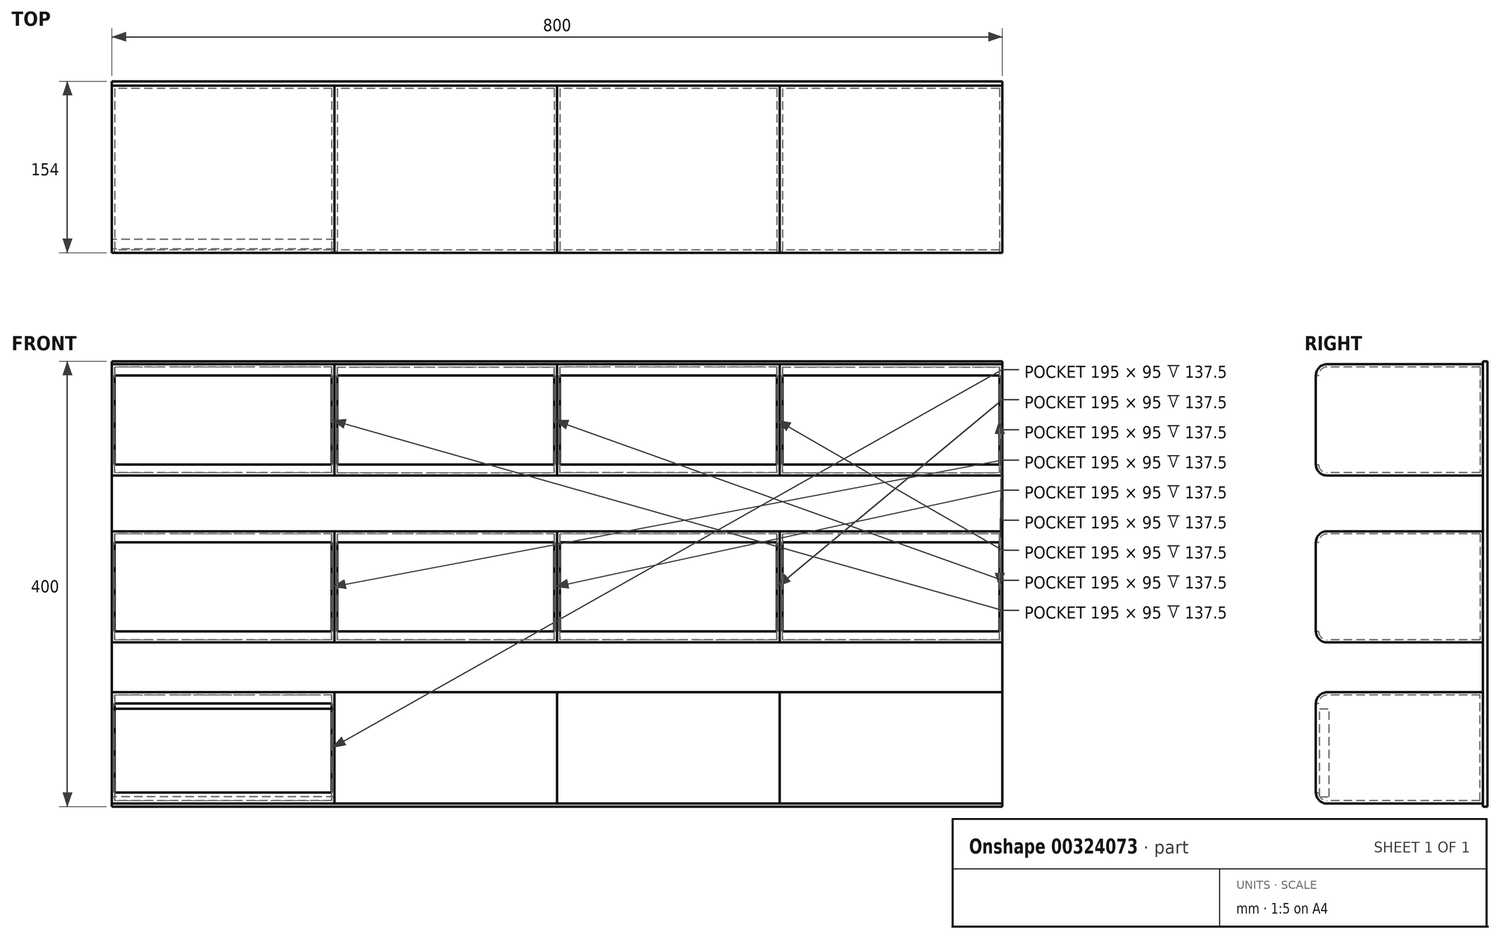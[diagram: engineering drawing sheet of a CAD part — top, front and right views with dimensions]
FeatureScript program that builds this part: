
annotation { "Feature Type Name" : "Feature", "Feature Type Description" : "" }
export const myFeature = defineFeature(function(context is Context, id is Id, definition is map)
    precondition{}
    {
        {
            var Q0;
            Q0=qCreatedBy(makeId("Front.planeOp"),FACE);
            var sketch = newSketch(context, id + "F0", { "sketchPlane" : qUnion([Q0])});
            skLineSegment(sketch, "E0.bottom", {"start": v(-400, 200) * mm, "end": v(400, 200) * mm});
            skLineSegment(sketch, "E0.top", {"start": v(-400, -200) * mm, "end": v(400, -200) * mm});
            skLineSegment(sketch, "E0.left", {"start": v(-400, 200) * mm, "end": v(-400, -200) * mm});
            skLineSegment(sketch, "E0.right", {"start": v(400, 200) * mm, "end": v(400, -200) * mm});
            skPoint(sketch, "E0.middle", {"position": v(0, 0) * mm});
            skSolve(sketch);
        }
        {
            var Q0;
            Q0=makeQuery(id+"F0.imprint","IMPRINT",FACE,{"disambiguationData":[TD([[makeQuery(id+"F0.imprint","IMPRINT",EDGE,{"derivedFrom":sQuery(id+"F0.wireOp",EDGE,"E0.bottom")}),-1.0]])]});
            extrude(context, id + "F1", {"entities" : qUnion([Q0]), "depth" : 4 * mm});
        }
        {
            var Q0;
            Q0=qCreatedBy(makeId("Right.planeOp"),FACE);
            cPlane(context, id + "F2", {"entities" : qUnion([Q0]), "cplaneType" : CPlaneType.OFFSET, "offset" : 400 * mm, "oppositeDirection" : true, "width" : 150 * mm, "height" : 150 * mm});
        }
        {
            var Q0;
            Q0=qCreatedBy(id+"F2.planeOp",FACE);
            var sketch = newSketch(context, id + "F3", { "sketchPlane" : qUnion([Q0])});
            skLineSegment(sketch, "E1.bottom", {"start": v(-4, -197.36) * mm, "end": v(-144, -197.36) * mm});
            skLineSegment(sketch, "E1.top", {"start": v(-4, -97.36) * mm, "end": v(-144, -97.36) * mm});
            skLineSegment(sketch, "E1.left", {"start": v(-4, -197.36) * mm, "end": v(-4, -97.36) * mm});
            skLineSegment(sketch, "E1.right", {"start": v(-154, -187.36) * mm, "end": v(-154, -107.36) * mm});
            skPoint(sketch, "E2.visualSharp", {"position": v(-154, -97.36) * mm});
            skArc(sketch, "E2.filletArc", {"start": v(-144, -97.36) * mm, "mid": v(-151.07, -100.3) * mm, "end": v(-154, -107.36) * mm});
            skPoint(sketch, "E3.visualSharp", {"position": v(-154, -197.36) * mm});
            skArc(sketch, "E3.filletArc", {"start": v(-154, -187.36) * mm, "mid": v(-151.07, -194.43) * mm, "end": v(-144, -197.36) * mm});
            skSolve(sketch);
        }
        {
            var Q0;
            Q0=makeQuery(id+"F3.imprint","IMPRINT",FACE,{"disambiguationData":[TD([[makeQuery(id+"F3.imprint","IMPRINT",EDGE,{"derivedFrom":sQuery(id+"F3.wireOp",EDGE,"E1.bottom")}),-1.0]])]});
            extrude(context, id + "F4", {"entities" : qUnion([Q0]), "depth" : 200 * mm});
        }
        {
            var Q0;
            Q0=qCreatedBy(id+"F2.planeOp",FACE);
            cPlane(context, id + "F5", {"entities" : qUnion([Q0]), "cplaneType" : CPlaneType.OFFSET, "offset" : 200 * mm, "width" : 150 * mm, "height" : 150 * mm});
        }
        {
            var Q0;
            Q0=makeQuery(id+"F4.opExtrude","SWEPT_BODY",BODY,{"disambiguationData":[OSD([sQuery(id+"F3.wireOp",EDGE,"E1.bottom"),sQuery(id+"F3.wireOp",EDGE,"E1.top"),sQuery(id+"F3.wireOp",EDGE,"E1.left"),sQuery(id+"F3.wireOp",EDGE,"E1.right"),sQuery(id+"F3.wireOp",EDGE,"E2.filletArc"),sQuery(id+"F3.wireOp",EDGE,"E3.filletArc")])]});
            var Q1;
            Q1=qCreatedBy(id+"F5.planeOp",FACE);
            mirror(context, id + "F6", {"entities" : qUnion([Q0]), "mirrorPlane" : qUnion([Q1])});
        }
        {
            var Q0;
            Q0=qCreatedBy(id+"F2.planeOp",FACE);
            cPlane(context, id + "F7", {"entities" : qUnion([Q0]), "cplaneType" : CPlaneType.OFFSET, "offset" : 400 * mm, "width" : 150 * mm, "height" : 150 * mm});
        }
        {
            var Q0;
            Q0=makeQuery(id+"F6.opPattern","COPY",BODY,{"derivedFrom":makeQuery(id+"F4.opExtrude","SWEPT_BODY",BODY,{"disambiguationData":[OSD([sQuery(id+"F3.wireOp",EDGE,"E1.bottom"),sQuery(id+"F3.wireOp",EDGE,"E1.top"),sQuery(id+"F3.wireOp",EDGE,"E1.left"),sQuery(id+"F3.wireOp",EDGE,"E1.right"),sQuery(id+"F3.wireOp",EDGE,"E2.filletArc"),sQuery(id+"F3.wireOp",EDGE,"E3.filletArc")])]}),"instanceName":"1"});
            var Q1;
            Q1=qCreatedBy(id+"F7.planeOp",FACE);
            mirror(context, id + "F8", {"entities" : qUnion([Q0]), "mirrorPlane" : qUnion([Q1])});
        }
        {
            var Q0;
            Q0=qCreatedBy(id+"F2.planeOp",FACE);
            cPlane(context, id + "F9", {"entities" : qUnion([Q0]), "cplaneType" : CPlaneType.OFFSET, "offset" : 600 * mm, "width" : 150 * mm, "height" : 150 * mm});
        }
        {
            var Q0;
            Q0=makeQuery(id+"F8.opPattern","COPY",BODY,{"derivedFrom":makeQuery(id+"F6.opPattern","COPY",BODY,{"derivedFrom":makeQuery(id+"F4.opExtrude","SWEPT_BODY",BODY,{"disambiguationData":[OSD([sQuery(id+"F3.wireOp",EDGE,"E1.bottom"),sQuery(id+"F3.wireOp",EDGE,"E1.top"),sQuery(id+"F3.wireOp",EDGE,"E1.left"),sQuery(id+"F3.wireOp",EDGE,"E1.right"),sQuery(id+"F3.wireOp",EDGE,"E2.filletArc"),sQuery(id+"F3.wireOp",EDGE,"E3.filletArc")])]}),"instanceName":"1"}),"instanceName":"1"});
            var Q1;
            Q1=qCreatedBy(id+"F9.planeOp",FACE);
            mirror(context, id + "F10", {"entities" : qUnion([Q0]), "mirrorPlane" : qUnion([Q1])});
        }
        {
            var Q0;
            Q0=makeQuery(id+"F4.opExtrude","SWEPT_FACE",FACE,{"disambiguationData":[OSD([sQuery(id+"F3.wireOp",EDGE,"E1.right")])]});
            shell(context, id + "F11", {"entities" : qUnion([Q0]), "thickness" : 2.5 * mm});
        }
        {
            var Q0;
            Q0=qCreatedBy(makeId("Right.planeOp"),FACE);
            cPlane(context, id + "F12", {"entities" : qUnion([Q0]), "cplaneType" : CPlaneType.OFFSET, "offset" : 400 * mm, "oppositeDirection" : true, "width" : 150 * mm, "height" : 150 * mm});
        }
        {
            var Q0;
            Q0=qCreatedBy(id+"F2.planeOp",FACE);
            var sketch = newSketch(context, id + "F13", { "sketchPlane" : qUnion([Q0])});
            skLineSegment(sketch, "E4.bottom", {"start": v(-150.65, -191.15) * mm, "end": v(-141.94, -191.15) * mm});
            skLineSegment(sketch, "E4.top", {"start": v(-150.65, -112.05) * mm, "end": v(-141.94, -112.05) * mm});
            skLineSegment(sketch, "E4.left", {"start": v(-150.65, -191.15) * mm, "end": v(-150.65, -112.05) * mm});
            skLineSegment(sketch, "E4.right", {"start": v(-141.94, -191.15) * mm, "end": v(-141.94, -112.05) * mm});
            skSolve(sketch);
        }
        {
            var Q0;
            Q0 = qSketchRegion(id + "F13", true);
            extrude(context, id + "F14", {"entities" : qUnion([Q0]), "depth" : 200 * mm});
        }
        {
            var Q0;
            Q0=makeQuery(id+"F4.opExtrude","SWEPT_BODY",BODY,{"disambiguationData":[OSD([sQuery(id+"F3.wireOp",EDGE,"E1.bottom"),sQuery(id+"F3.wireOp",EDGE,"E1.top"),sQuery(id+"F3.wireOp",EDGE,"E1.left"),sQuery(id+"F3.wireOp",EDGE,"E1.right"),sQuery(id+"F3.wireOp",EDGE,"E2.filletArc"),sQuery(id+"F3.wireOp",EDGE,"E3.filletArc")])]});
            var Q1;
            Q1=qCreatedBy(makeId("Top.planeOp"),FACE);
            mirror(context, id + "F15", {"entities" : qUnion([Q0]), "mirrorPlane" : qUnion([Q1])});
        }
        {
            var Q0;
            Q0=qCreatedBy(makeId("Right.planeOp"),FACE);
            cPlane(context, id + "F16", {"entities" : qUnion([Q0]), "cplaneType" : CPlaneType.OFFSET, "offset" : 200 * mm, "oppositeDirection" : true, "width" : 150 * mm, "height" : 150 * mm});
        }
        {
            var Q0;
            Q0=makeQuery(id+"F15.opPattern","COPY",BODY,{"derivedFrom":makeQuery(id+"F4.opExtrude","SWEPT_BODY",BODY,{"disambiguationData":[OSD([sQuery(id+"F3.wireOp",EDGE,"E1.bottom"),sQuery(id+"F3.wireOp",EDGE,"E1.top"),sQuery(id+"F3.wireOp",EDGE,"E1.left"),sQuery(id+"F3.wireOp",EDGE,"E1.right"),sQuery(id+"F3.wireOp",EDGE,"E2.filletArc"),sQuery(id+"F3.wireOp",EDGE,"E3.filletArc")])]}),"instanceName":"1"});
            var Q1;
            Q1=qCreatedBy(id+"F16.planeOp",FACE);
            mirror(context, id + "F17", {"entities" : qUnion([Q0]), "mirrorPlane" : qUnion([Q1])});
        }
        {
            var Q0;
            Q0=qCreatedBy(id+"F12.planeOp",FACE);
            cPlane(context, id + "F18", {"entities" : qUnion([Q0]), "cplaneType" : CPlaneType.OFFSET, "offset" : 400 * mm, "width" : 150 * mm, "height" : 150 * mm});
        }
        {
            var Q0;
            Q0=makeQuery(id+"F17.opPattern","COPY",BODY,{"derivedFrom":makeQuery(id+"F15.opPattern","COPY",BODY,{"derivedFrom":makeQuery(id+"F4.opExtrude","SWEPT_BODY",BODY,{"disambiguationData":[OSD([sQuery(id+"F3.wireOp",EDGE,"E1.bottom"),sQuery(id+"F3.wireOp",EDGE,"E1.top"),sQuery(id+"F3.wireOp",EDGE,"E1.left"),sQuery(id+"F3.wireOp",EDGE,"E1.right"),sQuery(id+"F3.wireOp",EDGE,"E2.filletArc"),sQuery(id+"F3.wireOp",EDGE,"E3.filletArc")])]}),"instanceName":"1"}),"instanceName":"1"});
            var Q1;
            Q1=qCreatedBy(id+"F18.planeOp",FACE);
            mirror(context, id + "F19", {"entities" : qUnion([Q0]), "mirrorPlane" : qUnion([Q1])});
        }
        {
            var Q0;
            Q0=qCreatedBy(id+"F12.planeOp",FACE);
            cPlane(context, id + "F20", {"entities" : qUnion([Q0]), "cplaneType" : CPlaneType.OFFSET, "offset" : 600 * mm, "width" : 150 * mm, "height" : 150 * mm});
        }
        {
            var Q0;
            Q0=makeQuery(id+"F19.opPattern","COPY",BODY,{"derivedFrom":makeQuery(id+"F17.opPattern","COPY",BODY,{"derivedFrom":makeQuery(id+"F15.opPattern","COPY",BODY,{"derivedFrom":makeQuery(id+"F4.opExtrude","SWEPT_BODY",BODY,{"disambiguationData":[OSD([sQuery(id+"F3.wireOp",EDGE,"E1.bottom"),sQuery(id+"F3.wireOp",EDGE,"E1.top"),sQuery(id+"F3.wireOp",EDGE,"E1.left"),sQuery(id+"F3.wireOp",EDGE,"E1.right"),sQuery(id+"F3.wireOp",EDGE,"E2.filletArc"),sQuery(id+"F3.wireOp",EDGE,"E3.filletArc")])]}),"instanceName":"1"}),"instanceName":"1"}),"instanceName":"1"});
            var Q1;
            Q1=qCreatedBy(id+"F20.planeOp",FACE);
            mirror(context, id + "F21", {"entities" : qUnion([Q0]), "mirrorPlane" : qUnion([Q1])});
        }
        {
            var Q0;
            Q0=makeQuery(id+"F15.opPattern","COPY",BODY,{"derivedFrom":makeQuery(id+"F4.opExtrude","SWEPT_BODY",BODY,{"disambiguationData":[OSD([sQuery(id+"F3.wireOp",EDGE,"E1.bottom"),sQuery(id+"F3.wireOp",EDGE,"E1.top"),sQuery(id+"F3.wireOp",EDGE,"E1.left"),sQuery(id+"F3.wireOp",EDGE,"E1.right"),sQuery(id+"F3.wireOp",EDGE,"E2.filletArc"),sQuery(id+"F3.wireOp",EDGE,"E3.filletArc")])]}),"instanceName":"1"});
            var Q1;
            Q1=makeQuery(id+"F1.opExtrude","CAP_EDGE",EDGE,{"disambiguationData":[OSD([sQuery(id+"F0.wireOp",EDGE,"E0.left")])],"isStart":true});
            transform(context, id + "F22", {"entities" : qUnion([Q0]), "transformType" : TransformType.TRANSLATION_DISTANCE, "transformDirection" : qUnion([Q1]), "distance" : 150 * mm, "makeCopy" : true});
        }
        {
            var Q0;
            Q0=makeQuery(id+"F22.opPattern","COPY",BODY,{"derivedFrom":makeQuery(id+"F15.opPattern","COPY",BODY,{"derivedFrom":makeQuery(id+"F4.opExtrude","SWEPT_BODY",BODY,{"disambiguationData":[OSD([sQuery(id+"F3.wireOp",EDGE,"E1.bottom"),sQuery(id+"F3.wireOp",EDGE,"E1.top"),sQuery(id+"F3.wireOp",EDGE,"E1.left"),sQuery(id+"F3.wireOp",EDGE,"E1.right"),sQuery(id+"F3.wireOp",EDGE,"E2.filletArc"),sQuery(id+"F3.wireOp",EDGE,"E3.filletArc")])]}),"instanceName":"1"}),"instanceName":"1"});
            transform(context, id + "F23", {"entities" : qUnion([Q0]), "transformType" : TransformType.TRANSLATION_3D, "dx" : 200 * mm, "dy" : 0 * mm, "dz" : 0 * mm, "makeCopy" : true});
        }
        {
            var Q0;
            Q0=makeQuery(id+"F23.opPattern","COPY",BODY,{"derivedFrom":makeQuery(id+"F22.opPattern","COPY",BODY,{"derivedFrom":makeQuery(id+"F15.opPattern","COPY",BODY,{"derivedFrom":makeQuery(id+"F4.opExtrude","SWEPT_BODY",BODY,{"disambiguationData":[OSD([sQuery(id+"F3.wireOp",EDGE,"E1.bottom"),sQuery(id+"F3.wireOp",EDGE,"E1.top"),sQuery(id+"F3.wireOp",EDGE,"E1.left"),sQuery(id+"F3.wireOp",EDGE,"E1.right"),sQuery(id+"F3.wireOp",EDGE,"E2.filletArc"),sQuery(id+"F3.wireOp",EDGE,"E3.filletArc")])]}),"instanceName":"1"}),"instanceName":"1"}),"instanceName":"1"});
            transform(context, id + "F24", {"entities" : qUnion([Q0]), "transformType" : TransformType.TRANSLATION_3D, "dx" : 200 * mm, "dy" : 0 * mm, "dz" : 0 * mm, "makeCopy" : true});
        }
        {
            var Q0;
            Q0=makeQuery(id+"F24.opPattern","COPY",BODY,{"derivedFrom":makeQuery(id+"F23.opPattern","COPY",BODY,{"derivedFrom":makeQuery(id+"F22.opPattern","COPY",BODY,{"derivedFrom":makeQuery(id+"F15.opPattern","COPY",BODY,{"derivedFrom":makeQuery(id+"F4.opExtrude","SWEPT_BODY",BODY,{"disambiguationData":[OSD([sQuery(id+"F3.wireOp",EDGE,"E1.bottom"),sQuery(id+"F3.wireOp",EDGE,"E1.top"),sQuery(id+"F3.wireOp",EDGE,"E1.left"),sQuery(id+"F3.wireOp",EDGE,"E1.right"),sQuery(id+"F3.wireOp",EDGE,"E2.filletArc"),sQuery(id+"F3.wireOp",EDGE,"E3.filletArc")])]}),"instanceName":"1"}),"instanceName":"1"}),"instanceName":"1"}),"instanceName":"1"});
            transform(context, id + "F25", {"entities" : qUnion([Q0]), "transformType" : TransformType.TRANSLATION_3D, "dx" : 200 * mm, "dy" : 0 * mm, "dz" : 0 * mm, "makeCopy" : true});
        }
    });
